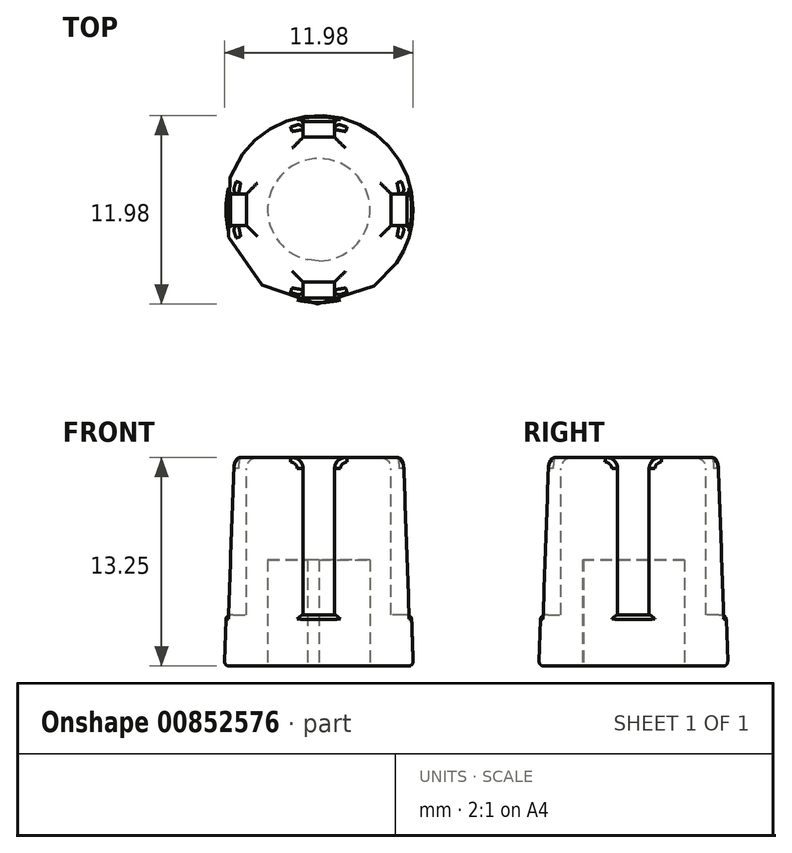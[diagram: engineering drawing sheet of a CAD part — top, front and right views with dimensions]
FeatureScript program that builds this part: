
annotation { "Feature Type Name" : "Feature", "Feature Type Description" : "" }
export const myFeature = defineFeature(function(context is Context, id is Id, definition is map)
    precondition{}
    {
        {
            var Q0;
            Q0=qCreatedBy(makeId("Top.planeOp"),FACE);
            var sketch = newSketch(context, id + "F0", { "sketchPlane" : qUnion([Q0])});
            skCircle(sketch, "E0", {"center": v(0, 0) * mm, "radius": 6 * mm});
            skArc(sketch, "E1", {"start": v(0, -3.25) * mm, "mid": v(0.36, 3.23) * mm, "end": v(-0.7, -3.17) * mm});
            skLineSegment(sketch, "E2", {"start": v(0, -3.25) * mm, "end": v(-0.7, -3.17) * mm});
            skSolve(sketch);
        }
        {
            var Q0;
            Q0=makeQuery(id+"F0.imprint","IMPRINT",FACE,{"disambiguationData":[TD([[makeQuery(id+"F0.imprint","IMPRINT",EDGE,{"derivedFrom":sQuery(id+"F0.wireOp",EDGE,"E0")}),1.0]])]});
            var Q1;
            Q1=makeQuery(id+"F0.imprint","IMPRINT",FACE,{"disambiguationData":[TD([[makeQuery(id+"F0.imprint","IMPRINT",EDGE,{"derivedFrom":sQuery(id+"F0.wireOp",EDGE,"E1")}),1.0]])]});
            extrude(context, id + "F1", {"entities" : qUnion([Q0, Q1]), "depth" : 13.25 * mm, "offsetDistance" : 25 * mm, "hasDraft" : true, "draftAngle" : 2 * degree, "draftPullDirection" : true});
        }
        {
            var Q0;
            Q0=makeQuery(id+"F0.imprint","IMPRINT",FACE,{"disambiguationData":[TD([[makeQuery(id+"F0.imprint","IMPRINT",EDGE,{"derivedFrom":sQuery(id+"F0.wireOp",EDGE,"E1")}),1.0]])]});
            extrude(context, id + "F2", {"entities" : qUnion([Q0]), "operationType" : NewBodyOperationType.REMOVE, "depth" : 6.75 * mm, "offsetDistance" : 25 * mm});
        }
        {
            var Q0;
            Q0=makeQuery(id+"F1.opExtrude","CAP_FACE",FACE,{"disambiguationData":[OSD([sQuery(id+"F0.wireOp",EDGE,"E0")])],"isStart":false});
            var sketch = newSketch(context, id + "F3", { "sketchPlane" : qUnion([Q0])});
            skLineSegment(sketch, "E3.bottom", {"start": v(-1, 5.6) * mm, "end": v(1, 5.6) * mm});
            skLineSegment(sketch, "E3.top", {"start": v(-1, 4.6) * mm, "end": v(1, 4.6) * mm});
            skLineSegment(sketch, "E3.left", {"start": v(-1, 5.6) * mm, "end": v(-1, 4.6) * mm});
            skLineSegment(sketch, "E3.right", {"start": v(1, 5.6) * mm, "end": v(1, 4.6) * mm});
            skLineSegment(sketch, "E4.1.0", {"start": v(-4.6, -1) * mm, "end": v(-4.6, 1) * mm});
            skLineSegment(sketch, "E4.1.1", {"start": v(-5.6, -1) * mm, "end": v(-4.6, -1) * mm});
            skLineSegment(sketch, "E4.1.2", {"start": v(-5.6, -1) * mm, "end": v(-5.6, 1) * mm});
            skLineSegment(sketch, "E4.1.3", {"start": v(-5.6, 1) * mm, "end": v(-4.6, 1) * mm});
            skLineSegment(sketch, "E4.2.0", {"start": v(1, -4.6) * mm, "end": v(-1, -4.6) * mm});
            skLineSegment(sketch, "E4.2.1", {"start": v(1, -5.6) * mm, "end": v(1, -4.6) * mm});
            skLineSegment(sketch, "E4.2.2", {"start": v(1, -5.6) * mm, "end": v(-1, -5.6) * mm});
            skLineSegment(sketch, "E4.2.3", {"start": v(-1, -5.6) * mm, "end": v(-1, -4.6) * mm});
            skLineSegment(sketch, "E4.3.0", {"start": v(4.6, 1) * mm, "end": v(4.6, -1) * mm});
            skLineSegment(sketch, "E4.3.1", {"start": v(5.6, 1) * mm, "end": v(4.6, 1) * mm});
            skLineSegment(sketch, "E4.3.2", {"start": v(5.6, 1) * mm, "end": v(5.6, -1) * mm});
            skLineSegment(sketch, "E4.3.3", {"start": v(5.6, -1) * mm, "end": v(4.6, -1) * mm});
            skPoint(sketch, "E4.center", {"position": v(0, 0) * mm});
            skSolve(sketch);
        }
        {
            var Q0;
            {var subQ0=sQuery(id+"F3.wireOp",EDGE,"E4.1.0");Q0=makeQuery(id+"F3.imprint","IMPRINT",FACE,{"disambiguationData":[TD([[makeQuery(id+"F3.imprint","IMPRINT",EDGE,{"derivedFrom":subQ0}),1.0]])]});}
            var Q1;
            {var subQ0=sQuery(id+"F3.wireOp",EDGE,"E4.2.0");Q1=makeQuery(id+"F3.imprint","IMPRINT",FACE,{"disambiguationData":[TD([[makeQuery(id+"F3.imprint","IMPRINT",EDGE,{"derivedFrom":subQ0}),1.0]])]});}
            var Q2;
            {var subQ0=sQuery(id+"F3.wireOp",EDGE,"E3.top");Q2=makeQuery(id+"F3.imprint","IMPRINT",FACE,{"disambiguationData":[TD([[makeQuery(id+"F3.imprint","IMPRINT",EDGE,{"derivedFrom":subQ0}),1.0]])]});}
            var Q3;
            {var subQ0=sQuery(id+"F3.wireOp",EDGE,"E4.3.0");Q3=makeQuery(id+"F3.imprint","IMPRINT",FACE,{"disambiguationData":[TD([[makeQuery(id+"F3.imprint","IMPRINT",EDGE,{"derivedFrom":subQ0}),1.0]])]});}
            var Q4;
            {var subQ0=sQuery(id+"F3.wireOp",EDGE,"E4.3.2");Q4=makeQuery(id+"F3.imprint","IMPRINT",FACE,{"disambiguationData":[TD([[makeQuery(id+"F3.imprint","IMPRINT",EDGE,{"derivedFrom":subQ0}),-1.0]])]});}
            var Q5;
            {var subQ0=sQuery(id+"F3.wireOp",EDGE,"E4.2.2");Q5=makeQuery(id+"F3.imprint","IMPRINT",FACE,{"disambiguationData":[TD([[makeQuery(id+"F3.imprint","IMPRINT",EDGE,{"derivedFrom":subQ0}),-1.0]])]});}
            var Q6;
            {var subQ0=sQuery(id+"F3.wireOp",EDGE,"E4.1.2");Q6=makeQuery(id+"F3.imprint","IMPRINT",FACE,{"disambiguationData":[TD([[makeQuery(id+"F3.imprint","IMPRINT",EDGE,{"derivedFrom":subQ0}),-1.0]])]});}
            var Q7;
            {var subQ0=sQuery(id+"F3.wireOp",EDGE,"E3.bottom");Q7=makeQuery(id+"F3.imprint","IMPRINT",FACE,{"disambiguationData":[TD([[makeQuery(id+"F3.imprint","IMPRINT",EDGE,{"derivedFrom":subQ0}),-1.0]])]});}
            var Q8;
            Q8 = qSketchRegion(id + "F0", true);
            extrude(context, id + "F4", {"entities" : qUnion([Q0, Q1, Q2, Q3, Q4, Q5, Q6, Q7, Q8]), "operationType" : NewBodyOperationType.REMOVE, "oppositeDirection" : true, "depth" : 10 * mm, "offsetDistance" : 25 * mm});
        }
        {
            var Q0;
            Q0=makeQuery(id+"F1.opExtrude","SWEPT_FACE",FACE,{"disambiguationData":[OSD([sQuery(id+"F0.wireOp",EDGE,"E0")])]});
            fillet(context, id + "F5", {"entities" : qUnion([Q0]), "radius" : .3 * mm, "tangentPropagation" : true, "allowEdgeOverflow" : false});
        }
        {
            var Q0;
            Q0=makeQuery(id+"F1.opExtrude","CAP_FACE",FACE,{"disambiguationData":[OSD([sQuery(id+"F0.wireOp",EDGE,"E0")])],"isStart":false});
            fillet(context, id + "F6", {"entities" : qUnion([Q0]), "radius" : .7 * mm, "tangentPropagation" : true, "allowEdgeOverflow" : false});
        }
    });
